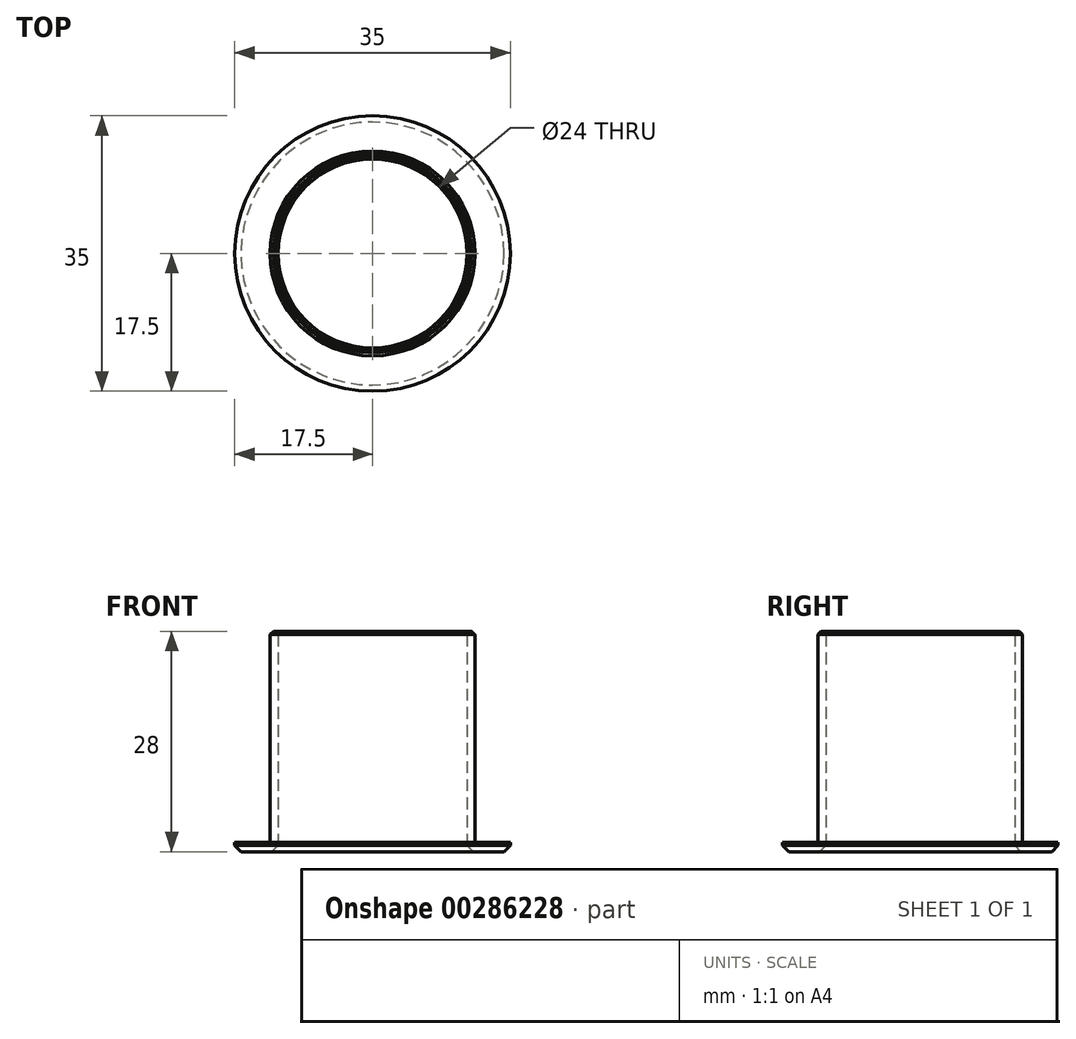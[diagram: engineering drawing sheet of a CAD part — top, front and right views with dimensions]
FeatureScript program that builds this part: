
annotation { "Feature Type Name" : "Feature", "Feature Type Description" : "" }
export const myFeature = defineFeature(function(context is Context, id is Id, definition is map)
    precondition{}
    {
        {
            var Q0;
            Q0=qCreatedBy(makeId("Top.planeOp"),FACE);
            var sketch = newSketch(context, id + "F0", { "sketchPlane" : qUnion([Q0])});
            skCircle(sketch, "E0", {"center": v(0, 0) * mm, "radius": 13 * mm});
            skCircle(sketch, "E1", {"center": v(0, 0) * mm, "radius": 17.5 * mm});
            skCircle(sketch, "E2", {"center": v(0, 0) * mm, "radius": 12 * mm});
            skSolve(sketch);
        }
        {
            var Q0;
            Q0=makeQuery(id+"F0.imprint","IMPRINT",FACE,{"disambiguationData":[TD([[makeQuery(id+"F0.imprint","IMPRINT",EDGE,{"derivedFrom":sQuery(id+"F0.wireOp",EDGE,"E0")}),1.0]])]});
            extrude(context, id + "F1", {"entities" : qUnion([Q0]), "flatOperationType" : FlatOperationType.REMOVE, "offsetDistance" : 25 * mm, "depth" : 28 * mm, "domain" : OperationDomain.MODEL});
        }
        {
            var Q0;
            Q0=makeQuery(id+"F0.imprint","IMPRINT",FACE,{"disambiguationData":[TD([[makeQuery(id+"F0.imprint","IMPRINT",EDGE,{"derivedFrom":sQuery(id+"F0.wireOp",EDGE,"E0")}),-1.0]])]});
            extrude(context, id + "F2", {"entities" : qUnion([Q0]), "operationType" : NewBodyOperationType.ADD, "depth" : 1.2 * mm});
        }
        {
            var Q0;
            {var subQ0=sQuery(id+"F0.wireOp",EDGE,"E0");Q0=makeQuery(id+"F2.boolean.opBoolean","MERGE",FACE,{"derivedFrom":[makeQuery(id+"F1.opExtrude","CAP_FACE",FACE,{"disambiguationData":[OSD([subQ0,sQuery(id+"F0.wireOp",EDGE,"E2")])],"isStart":true}),makeQuery(id+"F2.opExtrude","CAP_FACE",FACE,{"disambiguationData":[OSD([subQ0,sQuery(id+"F0.wireOp",EDGE,"E1")])],"isStart":true})]});}
            chamfer(context, id + "F3", {"entities" : qUnion([Q0]), "width" : .8 * mm, "tangentPropagation" : true});
        }
        {
            var Q0;
            Q0=makeQuery(id+"F1.opExtrude","CAP_FACE",FACE,{"disambiguationData":[OSD([sQuery(id+"F0.wireOp",EDGE,"E0"),sQuery(id+"F0.wireOp",EDGE,"E2")])],"isStart":false});
            chamfer(context, id + "F4", {"entities" : qUnion([Q0]), "width" : .4 * mm, "tangentPropagation" : true});
        }
    });
